# Revit family: MKH1-250-R3(R4)
name_source: partatom
category: Mechanical Equipment
revit_build: Autodesk Revit 2013 (Build: 20120221_2030(x64)
units: mm (PartAtom-declared; Revit-internal decimal feet)

## types (2) — shared parameters
Circuit breaker = 15 A
Condensation = water
Depth = 1020 mm
Description = High efficiency water cooled
Drain pipe = 18.5 mm
Height = 211 mm
Installation = Indoor installation
Liquid pipe = 19.05 mm
Machine material = Galvanized Steel
Manufacturer = Midea
Panel color = WH101
Power Input(H/M/L) = 47/26/14 W
Power supply = 220-240V ~50Hz/60Hz
Rated current = 0 A
Series = FCU
Width = 495 mm
clearance access behind = 50 mm  [stored 0.164042 ft]
clearance access down = 90 mm
clearance access left = 150 mm
clearance access right = 150 mm
clearance access up = 1500 mm  [stored 4.92126 ft]

## per-type parameters (varying)
| type | Air Flow(H/M/L) | Cooling Capacity(H/M/L) | Heating Capacity(H/M/L) | Net Weight |
| MKH1-250-R3 | 400/273/180 m3/h | 2.65/2.02/1.40 kW | 3.05/2.24/1.52 kW | 20.00 kg |
| MKH1-250-R4 | 425/284/184 m3/h | 3.05/2.26/1.63 kW | 3.15/2.09/1.38 kW | 20.80 kg |

note: column(s) folded — value = type name in every type: Model

note: [stored X ft] marks values corroborated as IEEE doubles in the binary element streams (Revit-internal decimal feet)

## geometry (parser evidence)
native form markers: Sweep x5
no freeform markers — native parametric forms only
